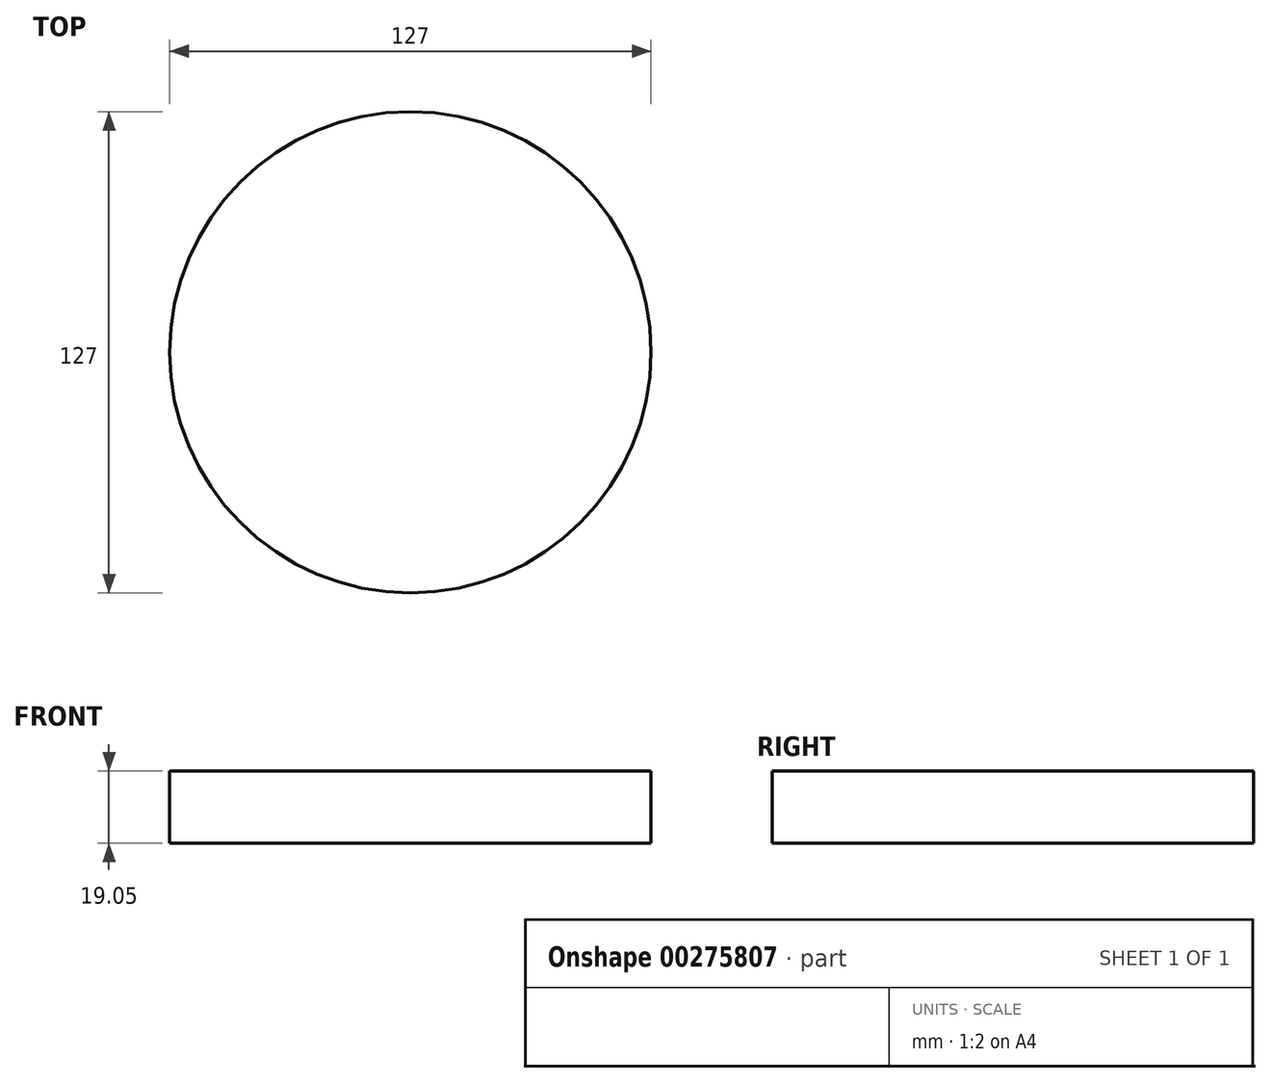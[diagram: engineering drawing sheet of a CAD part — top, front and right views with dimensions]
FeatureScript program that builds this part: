
annotation { "Feature Type Name" : "Feature", "Feature Type Description" : "" }
export const myFeature = defineFeature(function(context is Context, id is Id, definition is map)
    precondition{}
    {
        {
            var Q0;
            Q0=qCreatedBy(makeId("Top.planeOp"),FACE);
            var sketch = newSketch(context, id + "F0", { "sketchPlane" : qUnion([Q0])});
            skCircle(sketch, "E0", {"center": v(-111.4, 16.4) * mm, "radius": 63.5 * mm});
            skSolve(sketch);
        }
        {
            var Q0;
            Q0=makeQuery(id+"F0.imprint","IMPRINT",FACE,{"disambiguationData":[TD([[makeQuery(id+"F0.imprint","IMPRINT",EDGE,{"derivedFrom":sQuery(id+"F0.wireOp",EDGE,"E0")}),1.0]])]});
            extrude(context, id + "F1", {"entities" : qUnion([Q0]), "depth" : 19.05 * mm});
        }
    });
